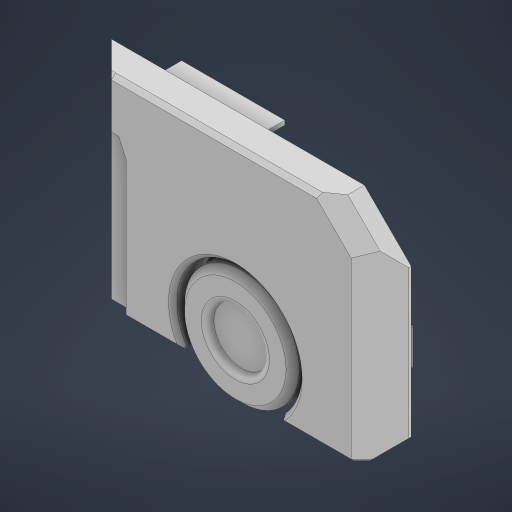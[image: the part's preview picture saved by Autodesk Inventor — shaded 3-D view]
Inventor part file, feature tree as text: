
AUTODESK INVENTOR PART (.ipt)
format: ipt  version: 2024 (Build 280153000, 153)  size: 1,250,304 bytes
history: native  units: in
note: dims shown in document units (in); Inventor stores cm internally (conversion verified against a paired STEP export)
features: reference x21, sketch x16, extrude x16, chamfer x13, projected_geometry x12, plane x6, other x3, fillet x1
ambient origin geometry x8: Origin, YZ Plane, XZ Plane, XY Plane, X Axis, Y Axis, Z Axis, Center Point
bodies: Solid1 (feature_tree)
feature tree (88):
  sketch  "Sketch1"  dims[d0=0.0157in d1=0.1181in]
  plane  "Work Plane1"
  extrude  "Extrusion1"  Depth=0.1181in
  sketch  "Sketch2"  dims[d2=1.0in d3=0.0in d4=0.7874in d6=0.2953in d7=2.3622in d9=0.2953in]
  plane  "Work Plane2"
  extrude  "Extrusion2"  Depth=0.7874in
  extrude  "Extrusion3"  Depth=3.1496in
  extrude  "Extrusion4"  Depth=0.1181in
  extrude  "Extrusion5"  Depth=0.1181in
  extrude  "Extrusion6"  Depth=1.0in TaperAngle=0.0deg
  chamfer  "Chamfer1"  Distance=0.0394in
  sketch  "Sketch7"  dims[d30=0.25in]
  plane  "Work Plane3"
  extrude  "Extrusion7"  Depth=0.0787in TaperAngle=0.0deg
  extrude  "Extrusion8"  Depth=0.125in TaperAngle=45.0deg
  chamfer  "Chamfer3"  Distance=0.4724in
  chamfer  "Chamfer5"  Distance=1.0in
  chamfer  "Chamfer7"  Distance=0.1575in
  extrude  "Extrusion10"  Depth=0.1969in TaperAngle=15.0deg
  fillet  "Fillet2"  Radius=0.8843in
  chamfer  "Chamfer8"  Distance=0.0787in Angle=15.0deg
  chamfer  "Chamfer9"  Distance=0.1181in
  chamfer  "Chamfer10"  Distance=0.1181in
  chamfer  "Chamfer11"  Distance=0.42in Angle=15.0deg
  chamfer  "Chamfer12"  Distance=0.545in Angle=15.0deg
  chamfer  "Chamfer13"  Distance=0.0787in Angle=15.0deg
  extrude  "Extrusion11"  Depth=0.1969in
  extrude  "Extrusion12"  Depth=0.1969in
  chamfer  "Chamfer14"  Distance=0.2756in
  extrude  "Extrusion13"  Depth=0.1969in TaperAngle=0.0deg
  chamfer  "Chamfer15"  Distance=0.1654in
  chamfer  "Chamfer16"  Distance=0.2756in
  sketch  "Sketch14"  dims[d41=0.4724in d42=0.0in d43=0.125in d44=0.125in d45=45.0deg]
  plane  "Work Plane4"
  extrude  "Extrusion14"  Depth=0.1969in
  sketch  "Sketch15"  dims[d46=0.0118in]
  plane  "Work Plane5"
  extrude  "Extrusion15"  Depth=0.1969in
  plane  "Work Plane6"
  extrude  "Extrusion16"  TaperAngle=45.0deg  [1 undecoded]
  extrude  "Extrusion17"  Depth=0.1969in TaperAngle=0.0deg
  reference  "Reference1"
  projected_geometry  "Projected Loop1"
  sketch  "Sketch3"  dims[d12=0.1952in d13=3.1496in d15=0.2953in d16=0.7874in d18=0.2953in]
  reference  "Reference2"
  reference  "Reference3"
  sketch  "Sketch4"  dims[d22=1.0in d23=0.0in d24=0.1181in]
  reference  "Reference4"
  reference  "Reference5"
  reference  "Reference6"
  reference  "Reference7"
  reference  "Reference8"
  reference  "Reference9"
  reference  "Reference10"
  sketch  "Sketch5"  dims[d25=0.1181in d26=0.1181in]
  projected_geometry  "Projected Loop2"
  sketch  "Sketch6"  dims[d27=0.1181in d28=1.0in d29=0.0in]
  projected_geometry  "Projected Loop3"
  projected_geometry  "Projected Loop4"
  reference  "Reference11"
  reference  "Reference12"
  reference  "Reference13"
  reference  "Reference14"
  reference  "Reference15"
  projected_geometry  "Projected Loop5"
  sketch  "Sketch8"  dims[d32=0.3937in]
  reference  "Reference16"
  reference  "Reference17"
  sketch  "Sketch10"  dims[d33=0.1181in]
  projected_geometry  "Projected Loop6"
  sketch  "Sketch11"  dims[d34=2.1654in]
  projected_geometry  "Projected Loop7"
  sketch  "Sketch12"  dims[d35=0.0984in d36=0.0394in d37=0.0in]
  projected_geometry  "Projected Loop8"
  sketch  "Sketch13"  dims[d38=0.1181in d39=0.0787in d40=0.0in]
  projected_geometry  "Projected Loop9"
  projected_geometry  "Projected Loop10"
  reference  "Reference19"
  reference  "Reference20"
  reference  "Reference21"
  reference  "Reference22"
  projected_geometry  "Projected Loop11"
  sketch  "Sketch16"  dims[d48=0.55in d49=0.4724in d50=0.0in d51=1.0in d52=0.0in]
  sketch  "Sketch17"  dims[d53=0.2756in d54=0.1575in d61=0.3912in d62=0.125in d63=15.0deg d67=0.8843in d68=0.125in d69=15.0deg d73=0.0787in d74=0.125in d75=15.0deg d76=0.1181in d77=0.0in d78=0.1181in d79=0.42in d80=0.125in d81=15.0deg d82=0.545in d83=0.125in d84=15.0deg d85=0.0787in d86=0.125in d87=15.0deg d88=2.1412in d89=0.125in d90=0.0344in d91=0.0787in d92=0.125in d93=0.0344in d94=0.2756in d95=0.125in d96=0.0344in d97=1.0in d98=0.0in d99=0.1654in d100=0.2756in d101=0.0in d102=0.0787in d103=0.125in d104=0.0344in d105=0.0787in d106=45.0deg d107=1.0in d108=0.0in d109=0.1969in d110=0.125in d111=0.0344in d112=0.0787in d113=0.125in d114=0.0344in d115=1.0in d116=0.0in d117=0.0118in d118=1.0in d119=0.0in d120=135.0deg d121=2.5349in d122=0.0in d123=0.2756in d124=2.0in d125=0.1969in d126=0.0in]
  projected_geometry  "Projected Loop12"
  other  "<userpath>\Desktop\SeniorDesign\Head_V3\Head_V3_Assembly.iam"
  other  "Head_V3_Assembly.iam"
  other  "Head_base_mount:1"
note: 1 required parameter value undecoded (feature->parameter linkage not recoverable at this tier; creation-order binding heuristic only, values carry confidence <= 0.55)
